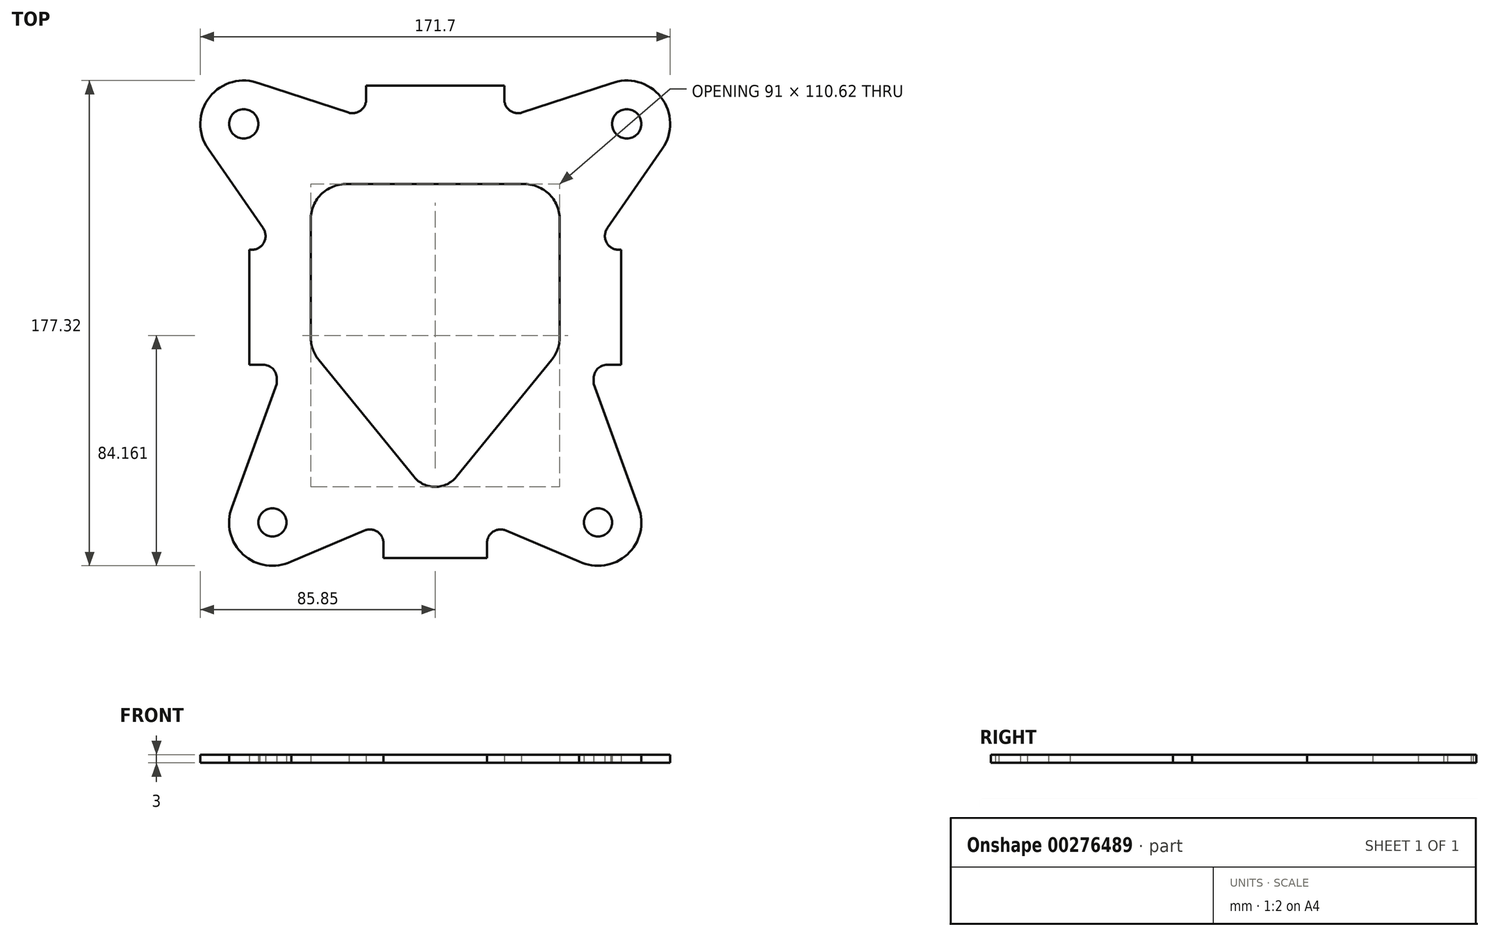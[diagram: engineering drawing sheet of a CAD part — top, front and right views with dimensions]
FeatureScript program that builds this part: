
annotation { "Feature Type Name" : "Feature", "Feature Type Description" : "" }
export const myFeature = defineFeature(function(context is Context, id is Id, definition is map)
    precondition{}
    {
        {
            var Q0;
            Q0=qCreatedBy(makeId("Top.planeOp"),FACE);
            var sketch = newSketch(context, id + "F0", { "sketchPlane" : qUnion([Q0])});
            skCircle(sketch, "E0", {"center": v(59.5, 0) * mm, "radius": 5.15 * mm});
            skCircle(sketch, "E1", {"center": v(70, 145.62) * mm, "radius": 5.35 * mm});
            skLineSegment(sketch, "E2", {"start": v(0, -13) * mm, "end": v(18.9, -13) * mm});
            skLineSegment(sketch, "E3", {"start": v(18.9, -13) * mm, "end": v(18.9, -7.55) * mm});
            skLineSegment(sketch, "E4", {"start": v(25.85, -2.94) * mm, "end": v(54.03, -14.88) * mm});
            skLineSegment(sketch, "E5", {"start": v(54.03, -14.88) * mm, "end": v(74.35, 5.55) * mm});
            skLineSegment(sketch, "E6", {"start": v(74.35, 5.55) * mm, "end": v(57.9, 50.62) * mm});
            skLineSegment(sketch, "E7", {"start": v(57.9, 50.62) * mm, "end": v(57.9, 52.62) * mm});
            skLineSegment(sketch, "E8", {"start": v(62.9, 57.62) * mm, "end": v(67.9, 57.62) * mm});
            skLineSegment(sketch, "E9", {"start": v(67.9, 57.62) * mm, "end": v(67.9, 99.62) * mm});
            skLineSegment(sketch, "E10", {"start": v(67.9, 99.62) * mm, "end": v(67.01, 99.62) * mm});
            skLineSegment(sketch, "E11", {"start": v(62.9, 107.46) * mm, "end": v(83.12, 136.73) * mm});
            skLineSegment(sketch, "E12", {"start": v(83.12, 136.73) * mm, "end": v(65.97, 160.95) * mm});
            skLineSegment(sketch, "E13", {"start": v(65.97, 160.95) * mm, "end": v(31.8, 149.77) * mm});
            skLineSegment(sketch, "E14", {"start": v(25.25, 154.52) * mm, "end": v(25.25, 159.62) * mm});
            skLineSegment(sketch, "E15", {"start": v(25.25, 159.62) * mm, "end": v(0, 159.62) * mm});
            skCircle(sketch, "E16", {"center": v(59.5, 0) * mm, "radius": 15.85 * mm});
            skCircle(sketch, "E17", {"center": v(70, 145.62) * mm, "radius": 15.85 * mm});
            skLineSegment(sketch, "E18", {"start": v(0, 123.62) * mm, "end": v(33.5, 123.62) * mm});
            skLineSegment(sketch, "E19", {"start": v(33.5, 123.62) * mm, "end": v(45.5, 110.76) * mm});
            skLineSegment(sketch, "E20", {"start": v(45.5, 110.76) * mm, "end": v(45.5, 67.63) * mm});
            skLineSegment(sketch, "E21", {"start": v(42.58, 59.41) * mm, "end": v(0, 7.17) * mm});
            skCircle(sketch, "E22", {"center": v(0, 23) * mm, "radius": 10 * mm});
            skCircle(sketch, "E23", {"center": v(32.5, 110.66) * mm, "radius": 13 * mm});
            skPoint(sketch, "E23.third.point", {"position": v(20.2, 106.46) * mm});
            skLineSegment(sketch, "E24.MirrorCS", {"start": v(-18.9, -13) * mm, "end": v(-18.9, -7.55) * mm});
            skLineSegment(sketch, "E25.MirrorCS", {"start": v(-25.25, 154.52) * mm, "end": v(-25.25, 159.62) * mm});
            skLineSegment(sketch, "E26.MirrorCS", {"start": v(0, -13) * mm, "end": v(-18.9, -13) * mm});
            skCircle(sketch, "E27.MirrorC", {"center": v(-59.5, 0) * mm, "radius": 15.85 * mm});
            skLineSegment(sketch, "E28.MirrorCS", {"start": v(0, 123.62) * mm, "end": v(-33.5, 123.62) * mm});
            skLineSegment(sketch, "E29.MirrorCS", {"start": v(-45.5, 110.76) * mm, "end": v(-45.5, 67.63) * mm});
            skLineSegment(sketch, "E30.MirrorCS", {"start": v(-83.12, 136.73) * mm, "end": v(-65.97, 160.95) * mm});
            skLineSegment(sketch, "E31.MirrorCS", {"start": v(-57.48, 99.62) * mm, "end": v(-83.12, 136.73) * mm});
            skLineSegment(sketch, "E32.MirrorCS", {"start": v(-54.03, -14.88) * mm, "end": v(-74.35, 5.55) * mm});
            skLineSegment(sketch, "E33.MirrorCS", {"start": v(-25.85, -2.94) * mm, "end": v(-54.03, -14.88) * mm});
            skLineSegment(sketch, "E34.MirrorCS", {"start": v(-74.35, 5.55) * mm, "end": v(-57.9, 50.62) * mm});
            skLineSegment(sketch, "E35.MirrorCS", {"start": v(-33.5, 123.62) * mm, "end": v(-45.5, 110.76) * mm});
            skLineSegment(sketch, "E36.MirrorCS", {"start": v(-42.58, 59.41) * mm, "end": v(0, 7.17) * mm});
            skPoint(sketch, "E37.MirrorP", {"position": v(-20.2, 106.46) * mm});
            skCircle(sketch, "E38.MirrorC", {"center": v(-70, 145.62) * mm, "radius": 15.85 * mm});
            skLineSegment(sketch, "E39.MirrorCS", {"start": v(-65.97, 160.95) * mm, "end": v(-31.8, 149.77) * mm});
            skCircle(sketch, "E40.MirrorC", {"center": v(-59.5, 0) * mm, "radius": 5.15 * mm});
            skLineSegment(sketch, "E41.MirrorCS", {"start": v(-25.25, 159.62) * mm, "end": v(0, 159.62) * mm});
            skCircle(sketch, "E42.MirrorC", {"center": v(-70, 145.62) * mm, "radius": 5.35 * mm});
            skCircle(sketch, "E43.MirrorC", {"center": v(-32.5, 110.66) * mm, "radius": 13 * mm});
            skPoint(sketch, "E44.visualSharp", {"position": v(18.9, 0) * mm});
            skArc(sketch, "E44.filletArc", {"start": v(25.85, -2.94) * mm, "mid": v(21.14, -3.38) * mm, "end": v(18.9, -7.55) * mm});
            skPoint(sketch, "E45.visualSharp", {"position": v(-18.9, 0) * mm});
            skArc(sketch, "E45.filletArc", {"start": v(-18.9, -7.55) * mm, "mid": v(-21.14, -3.38) * mm, "end": v(-25.85, -2.94) * mm});
            skPoint(sketch, "E46.visualSharp", {"position": v(57.9, 57.62) * mm});
            skArc(sketch, "E46.filletArc", {"start": v(62.9, 57.62) * mm, "mid": v(59.36, 56.16) * mm, "end": v(57.9, 52.62) * mm});
            skPoint(sketch, "E47.visualSharp", {"position": v(57.48, 99.62) * mm});
            skArc(sketch, "E47.filletArc", {"start": v(62.9, 107.46) * mm, "mid": v(62.59, 102.3) * mm, "end": v(67.01, 99.62) * mm});
            skPoint(sketch, "E48.visualSharp", {"position": v(25.25, 147.62) * mm});
            skArc(sketch, "E48.filletArc", {"start": v(25.25, 154.52) * mm, "mid": v(27.32, 150.47) * mm, "end": v(31.8, 149.77) * mm});
            skPoint(sketch, "E49.visualSharp", {"position": v(-25.25, 147.62) * mm});
            skArc(sketch, "E49.filletArc", {"start": v(-31.8, 149.77) * mm, "mid": v(-27.32, 150.47) * mm, "end": v(-25.25, 154.52) * mm});
            skLineSegment(sketch, "E50.MirrorCS", {"start": v(-67.9, 99.62) * mm, "end": v(-67.01, 99.62) * mm});
            skLineSegment(sketch, "E51.MirrorCS", {"start": v(-57.9, 50.62) * mm, "end": v(-57.9, 52.62) * mm});
            skLineSegment(sketch, "E52.MirrorCS", {"start": v(-67.9, 57.62) * mm, "end": v(-67.9, 99.62) * mm});
            skLineSegment(sketch, "E53.MirrorCS", {"start": v(-62.9, 57.62) * mm, "end": v(-67.9, 57.62) * mm});
            skArc(sketch, "E54.MirrorCS", {"start": v(-62.9, 57.62) * mm, "mid": v(-59.36, 56.16) * mm, "end": v(-57.9, 52.62) * mm});
            skPoint(sketch, "E55.MirrorP", {"position": v(-57.9, 57.62) * mm});
            skPoint(sketch, "E56.MirrorP", {"position": v(-57.48, 99.62) * mm});
            skArc(sketch, "E57.MirrorCS", {"start": v(-62.9, 107.46) * mm, "mid": v(-62.59, 102.3) * mm, "end": v(-67.01, 99.62) * mm});
            skPoint(sketch, "E58.visualSharp", {"position": v(45.5, 63) * mm});
            skArc(sketch, "E58.filletArc", {"start": v(42.58, 59.41) * mm, "mid": v(44.75, 63.27) * mm, "end": v(45.5, 67.63) * mm});
            skPoint(sketch, "E59.visualSharp", {"position": v(-45.5, 63) * mm});
            skArc(sketch, "E59.filletArc", {"start": v(-45.5, 67.63) * mm, "mid": v(-44.75, 63.27) * mm, "end": v(-42.58, 59.41) * mm});
            skLineSegment(sketch, "E60", {"start": v(25.85, -2.94) * mm, "end": v(61.48, 40.78) * mm, "construction": true});
            skLineSegment(sketch, "E61", {"start": v(37.36, -7.82) * mm, "end": v(66.12, 27.47) * mm, "construction": true});
            skPoint(sketch, "E61.endSnap0", {"position": v(66.12, 28.09) * mm});
            skLineSegment(sketch, "E62.MirrorCS", {"start": v(-25.85, -2.94) * mm, "end": v(-61.48, 40.78) * mm, "construction": true});
            skLineSegment(sketch, "E63.MirrorCS", {"start": v(-37.36, -7.82) * mm, "end": v(-66.12, 27.47) * mm, "construction": true});
            skSolve(sketch);
        }
        {
            var Q0;
            Q0 = qSketchRegion(id + "F0", true);
            var Q1;
            {var subQ0=sQuery(id+"F0.wireOp",EDGE,"E36.MirrorCS");var subQ1=sQuery(id+"F0.wireOp",EDGE,"E21");var subQ2=makeQuery(id+"F0.imprint","INTERSECT",VERTEX,{"derivedFrom":[subQ1,subQ0]});Q1=makeQuery(id+"F0.imprint","IMPRINT",FACE,{"disambiguationData":[TD([[makeQuery(id+"F0.imprint","IMPRINT",EDGE,{"disambiguationData":[TD([[subQ2,1.0]])],"derivedFrom":subQ1}),-1.0]])]});}
            extrude(context, id + "F1", {"entities" : qUnion([Q0, Q1]), "depth" : 3 * mm});
        }
    });
